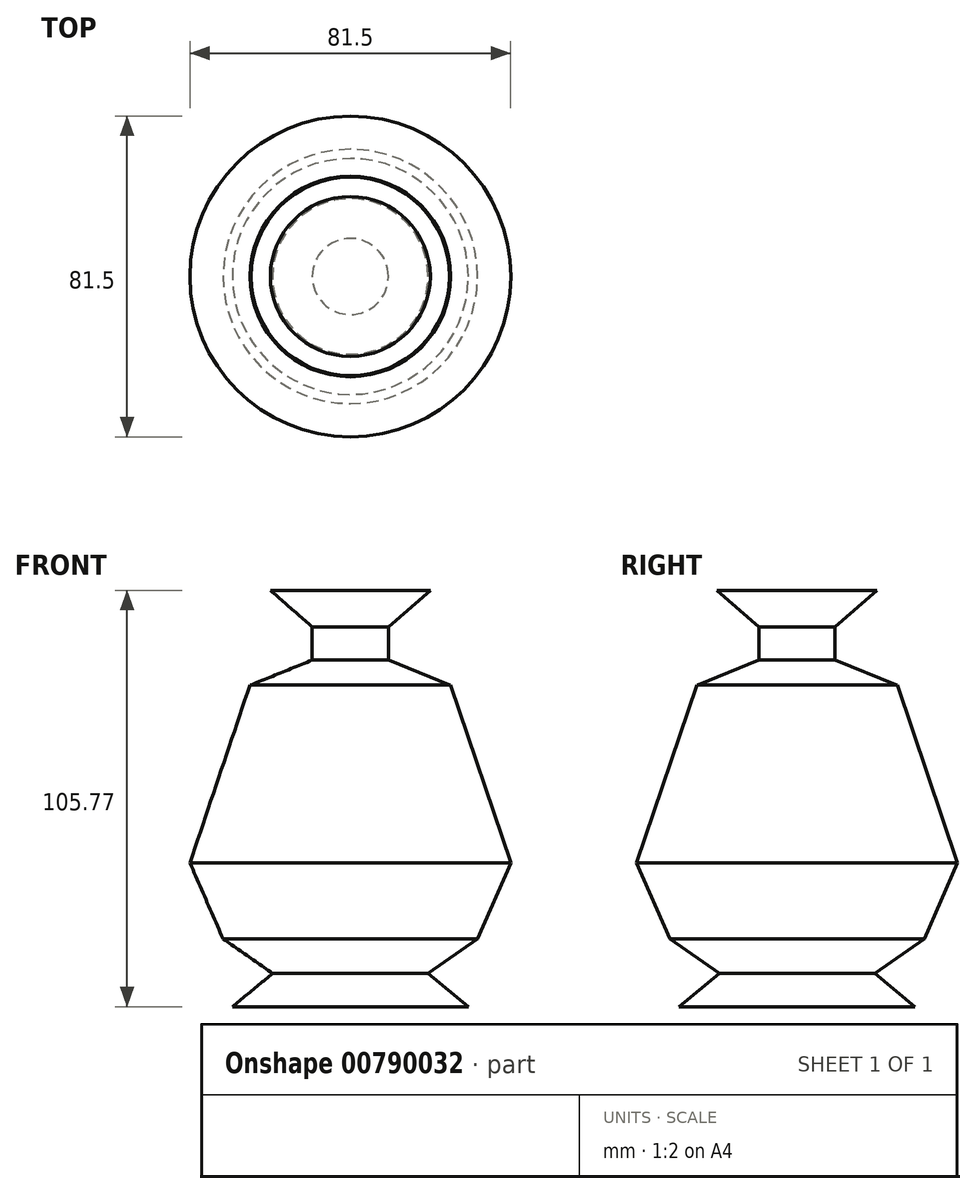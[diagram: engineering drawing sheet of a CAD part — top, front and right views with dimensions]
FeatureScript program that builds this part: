
annotation { "Feature Type Name" : "Feature", "Feature Type Description" : "" }
export const myFeature = defineFeature(function(context is Context, id is Id, definition is map)
    precondition{}
    {
        {
            var Q0;
            Q0=qCreatedBy(makeId("Front.planeOp"),FACE);
            var sketch = newSketch(context, id + "F0", { "sketchPlane" : qUnion([Q0])});
            skLineSegment(sketch, "E0", {"start": v(0, -41.98) * mm, "end": v(29.96, -41.98) * mm});
            skLineSegment(sketch, "E1", {"start": v(29.96, -41.98) * mm, "end": v(19.76, -33.53) * mm});
            skLineSegment(sketch, "E2", {"start": v(19.76, -33.53) * mm, "end": v(32.3, -24.8) * mm});
            skLineSegment(sketch, "E3", {"start": v(32.3, -24.8) * mm, "end": v(40.75, -5.45) * mm});
            skLineSegment(sketch, "E4", {"start": v(40.75, -5.45) * mm, "end": v(25.49, 39.8) * mm});
            skLineSegment(sketch, "E5", {"start": v(25.22, 39.8) * mm, "end": v(9.68, 46.07) * mm});
            skLineSegment(sketch, "E6", {"start": v(9.68, 46.07) * mm, "end": v(9.68, 54.52) * mm});
            skLineSegment(sketch, "E7", {"start": v(9.68, 54.52) * mm, "end": v(20.3, 63.79) * mm});
            skLineSegment(sketch, "E8", {"start": v(20.3, 63.79) * mm, "end": v(0, 63.79) * mm});
            skLineSegment(sketch, "E9", {"start": v(0, -41.98) * mm, "end": v(0, 63.79) * mm});
            skLineSegment(sketch, "E10", {"start": v(0, -68.15) * mm, "end": v(0, 70.87) * mm, "construction": true});
            skSolve(sketch);
        }
        {
            var Q0;
            Q0=sQuery(id+"F0.wireOp",EDGE,"E8");
            var Q1;
            Q1=sQuery(id+"F0.wireOp",EDGE,"E7");
            var Q2;
            Q2=sQuery(id+"F0.wireOp",EDGE,"E6");
            var Q3;
            Q3=sQuery(id+"F0.wireOp",EDGE,"E5");
            var Q4;
            Q4=sQuery(id+"F0.wireOp",EDGE,"E4");
            var Q5;
            Q5=sQuery(id+"F0.wireOp",EDGE,"E3");
            var Q6;
            Q6=sQuery(id+"F0.wireOp",EDGE,"E2");
            var Q7;
            Q7=sQuery(id+"F0.wireOp",EDGE,"E1");
            var Q8;
            Q8=sQuery(id+"F0.wireOp",EDGE,"E0");
            var Q9;
            Q9=sQuery(id+"F0.wireOp",EDGE,"E9");
            revolve(context, id + "F1", {"bodyType" : ToolBodyType.SURFACE, "surfaceOperationType" : NewSurfaceOperationType.NEW, "surfaceEntities" : qUnion([Q0, Q1, Q2, Q3, Q4, Q5, Q6, Q7, Q8]), "axis" : qUnion([Q9]), "revolveType" : RevolveType.FULL, "oppositeDirection" : true});
        }
    });
